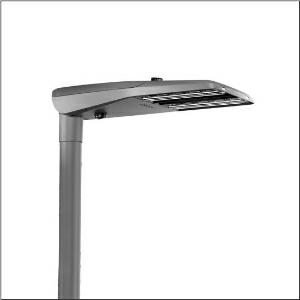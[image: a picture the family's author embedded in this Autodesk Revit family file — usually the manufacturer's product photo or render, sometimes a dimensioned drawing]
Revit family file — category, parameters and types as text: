
# Revit family: streetlight_sl_11_iq_midi___st1_0p1_0_5xc3k51y08me_73ea
name_source: partatom
category: Lighting Fixtures
units: mm (PartAtom-declared; Revit-internal decimal feet)

## family parameters
Cut with Voids When Loaded = No
Host = Face
Light Source = No
Part Type = Normal
Room Calculation Point = No
Round Connector Dimension = Use Diameter
Shared = No

## types (1)
- --- (1 x LED, 17540 lm, 122.7 W, 3000K)
    Apparent Load = 123 VA
    CIE Flux Codes = 32 65 95 100 100
    Color Rendering = 70
    Color Temperature = 3000K
    Default Elevation = 1800 mm
    Description = Streetlight SL 11 iQ midi, mast luminaire, primary light control with 3 zone facetted reflector, of plastic, silver coated, highly specular, primary optical cover: cover, of PMMA, transparent, light distribution: ST1.0P1.0, light emission: direct distribution, primary light characteristic: asymmetric, installation type: post-top, side-entry, lamps: LED, High Power LED, rated values: 17.540lm | 122,7W | 143lm/W (begin service life); end service life: 17.540lm | 130,2W; at 50% lumin. flux: 8.770lm | 56,1W | 156,3lm/W, colour temperature: 3000K, colour rendering: CRI > 70, light colour: 730, light setting 1 begin service life: 100% | 17.540lm | 122,7W | 143lm/W | 3.000K, light setting 1 end service life: 130,2W, further light settings possible, control: pre-setting: logarithmic dimming characteristic, Street-Remote, Auto-Match, Temp-Guard, Lumen-Switch, Night-Set, Smart-Wire, Light-Fading, Desk-Remote (wireless, voltage-free reading and setting of iQ features in the workshop via application-optimized NFC function/RFID function), optimised constant luminous flux control (CLO 2.0), with cable H07RN-F 3x 1.5mm², mains connection: 230..240V, AC, 50/60Hz, connection cable pre-assembled, cable length: 12,5m, luminaire housing, of diecast aluminium, powder-coated, SITECO metallic grey (DB 702S), please order mast flange separately, inclination adjustable without tools: 0°, 5°, 10°, 15° (post-top) | 0°, -5°, -10°, -15° (side-entry), sealing non-destructively replaceable, multi-level sealing system, length: 780mm, width: 376mm, height: 118mm, mast flange for spigot size: 42mm (side-entry): 5XC10008XM4, 60/48mm (side-entry/post-top): 5XC10108XM2, 76/60mm (side-entry/post-top): 5XC10108XM1, equipment: Power, Smart Interface below and above, protection rating (complete): IP66, insulation class (complete): insulation class II (safety insulation), certification: CE, ENEC, ENEC+, VDE, UKCA, impact resistance: IK10, permissible operating ambient temperature for outdoor applications: -25..+50°C, standard-compliant lighting for roads and squares, Environmental Product Declaration (EPD) tested and certified by an independent institute, packaging unit: 1 piece

Light Distribution: ST1.0P1.0
    Height = 118 mm
    Lamp = 1 x LED
    Lamp Light Flux = 17540 lm
    Lamp Power = 122.7 W
    Lamp count = 1
    Length = 780 mm
    Luminous efficacy = 143 lm/W
    Manufacturer = Siteco
    ModVariant = No
    Model = 5XC3K51Y08ME
    Number of Poles = 1
    OnlyDefault = Yes
    Power Factor = 1
    Product Name = Streetlight SL 11 iQ midi | ST1.0P1.0
    Product group = mast luminaire | pylon top
    ProductGroupID = 6100
    Protection Class = Protection class II
    Protection Degree = IP 66
    RLX_Detail_Level = 1
    RLX_Emergency_Light_Flux = 0 lm
    RLX_Emergency_Type = 0
    RLX_Emergency_Type_DB = No
    RlxData = <blob elided: 69977 chars, md5=6695fd24>
    Socket = socket
    Standby Power = 0 W
    System Light Flux = 17540 lm
    System Power = 123 W
    Type Comments = factory setting: luminous flux: 100 % | dim-lin: 254 | 553 mA
    Type Image = l_1004429.jpg
    URL = http://relux.com
    VarID = @adj_048037
    Voltage = 0 V
    Weight = 0.00 kg
    Width = 376 mm

## geometry (parser evidence)
native form markers: Blend x4, Sweep x8
no freeform markers — native parametric forms only
